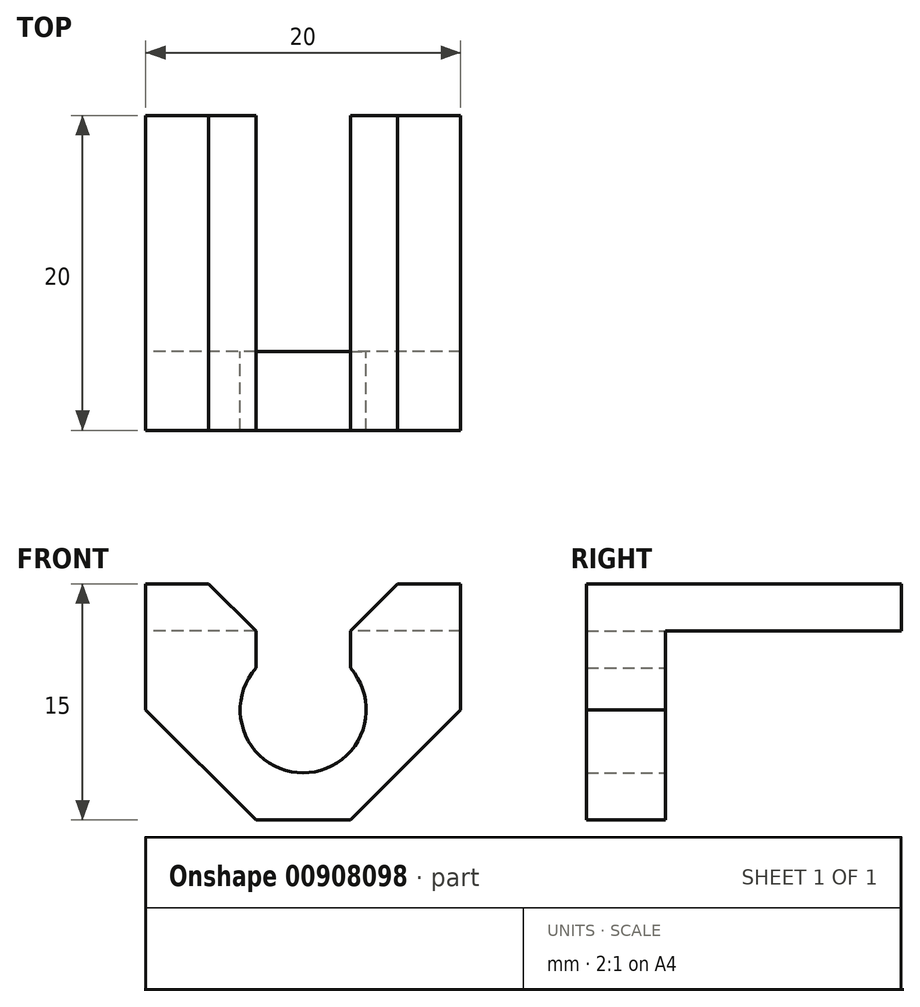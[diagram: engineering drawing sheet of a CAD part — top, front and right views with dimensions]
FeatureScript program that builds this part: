
annotation { "Feature Type Name" : "Feature", "Feature Type Description" : "" }
export const myFeature = defineFeature(function(context is Context, id is Id, definition is map)
    precondition{}
    {
        {
            var Q0;
            Q0=qCreatedBy(makeId("Front.planeOp"),FACE);
            var sketch = newSketch(context, id + "F0", { "sketchPlane" : qUnion([Q0])});
            skCircle(sketch, "E0", {"center": v(0, 0) * mm, "radius": 4 * mm});
            skLineSegment(sketch, "E1", {"start": v(0, -7) * mm, "end": v(10, -7) * mm});
            skLineSegment(sketch, "E2", {"start": v(10, -7) * mm, "end": v(10, 8) * mm});
            skLineSegment(sketch, "E3", {"start": v(10, 8) * mm, "end": v(3, 8) * mm});
            skLineSegment(sketch, "E4", {"start": v(3, 8) * mm, "end": v(3, 2.65) * mm});
            skLineSegment(sketch, "E5.MirrorCS", {"start": v(-3, 8) * mm, "end": v(-3, 2.65) * mm});
            skLineSegment(sketch, "E6.MirrorCS", {"start": v(-10, 8) * mm, "end": v(-3, 8) * mm});
            skLineSegment(sketch, "E7.MirrorCS", {"start": v(-10, -7) * mm, "end": v(-10, 8) * mm});
            skLineSegment(sketch, "E8.MirrorCS", {"start": v(0, -7) * mm, "end": v(-10, -7) * mm});
            skSolve(sketch);
        }
        {
            var Q0;
            Q0=makeQuery(id+"F0.imprint","IMPRINT",FACE,{"disambiguationData":[TD([[makeQuery(id+"F0.imprint","IMPRINT",EDGE,{"derivedFrom":sQuery(id+"F0.wireOp",EDGE,"E1")}),1.0]])]});
            extrude(context, id + "F1", {"entities" : qUnion([Q0]), "depth" : 5 * mm, "offsetDistance" : 25 * mm});
        }
        {
            var Q0;
            Q0=makeQuery(id+"F1.opExtrude","SWEPT_EDGE",EDGE,{"disambiguationData":[OSD([sQuery(id+"F0.wireOp",EDGE,"E7.MirrorCS"),sQuery(id+"F0.wireOp",EDGE,"E8.MirrorCS")])]});
            var Q1;
            Q1=makeQuery(id+"F1.opExtrude","SWEPT_EDGE",EDGE,{"disambiguationData":[OSD([sQuery(id+"F0.wireOp",EDGE,"E1"),sQuery(id+"F0.wireOp",EDGE,"E2")])]});
            chamfer(context, id + "F2", {"entities" : qUnion([Q0, Q1]), "width" : 7 * mm, "tangentPropagation" : true});
        }
        {
            var Q0;
            Q0=makeQuery(id+"F1.opExtrude","CAP_FACE",FACE,{"disambiguationData":[OSD([sQuery(id+"F0.wireOp",EDGE,"E0"),sQuery(id+"F0.wireOp",EDGE,"E1"),sQuery(id+"F0.wireOp",EDGE,"E2"),sQuery(id+"F0.wireOp",EDGE,"E3"),sQuery(id+"F0.wireOp",EDGE,"E4"),sQuery(id+"F0.wireOp",EDGE,"E5.MirrorCS"),sQuery(id+"F0.wireOp",EDGE,"E6.MirrorCS"),sQuery(id+"F0.wireOp",EDGE,"E7.MirrorCS"),sQuery(id+"F0.wireOp",EDGE,"E8.MirrorCS")])],"isStart":true});
            var sketch = newSketch(context, id + "F3", { "sketchPlane" : qUnion([Q0])});
            skLineSegment(sketch, "E9.0.0", {"start": v(-10, 8) * mm, "end": v(-10, 0) * mm});
            skLineSegment(sketch, "E9.0.1", {"start": v(-10, 0) * mm, "end": v(-3, -7) * mm});
            skLineSegment(sketch, "E9.0.2", {"start": v(-3, -7) * mm, "end": v(3, -7) * mm});
            skLineSegment(sketch, "E9.0.3", {"start": v(3, -7) * mm, "end": v(10, 0) * mm});
            skLineSegment(sketch, "E9.0.4", {"start": v(10, 0) * mm, "end": v(10, 8) * mm});
            skLineSegment(sketch, "E9.0.5", {"start": v(10, 8) * mm, "end": v(3, 8) * mm});
            skLineSegment(sketch, "E9.0.6", {"start": v(3, 8) * mm, "end": v(3, 2.65) * mm});
            skArc(sketch, "E9.0.7", {"start": v(3, 2.65) * mm, "mid": v(0, -4) * mm, "end": v(-3, 2.65) * mm});
            skLineSegment(sketch, "E9.0.8", {"start": v(-3, 2.65) * mm, "end": v(-3, 8) * mm});
            skLineSegment(sketch, "E9.0.9", {"start": v(-3, 8) * mm, "end": v(-10, 8) * mm});
            skLineSegment(sketch, "E10", {"start": v(-10, 5) * mm, "end": v(10, 5) * mm});
            skSolve(sketch);
        }
        {
            var Q0;
            {var subQ0=sQuery(id+"F3.wireOp",EDGE,"E9.0.9");Q0=makeQuery(id+"F3.imprint","IMPRINT",FACE,{"disambiguationData":[TD([[makeQuery(id+"F3.imprint","IMPRINT",EDGE,{"derivedFrom":subQ0}),-1.0]])]});}
            var Q1;
            {var subQ0=sQuery(id+"F3.wireOp",EDGE,"E9.0.5");Q1=makeQuery(id+"F3.imprint","IMPRINT",FACE,{"disambiguationData":[TD([[makeQuery(id+"F3.imprint","IMPRINT",EDGE,{"derivedFrom":subQ0}),1.0]])]});}
            extrude(context, id + "F4", {"entities" : qUnion([Q0, Q1]), "operationType" : NewBodyOperationType.ADD, "depth" : 15 * mm, "offsetDistance" : 25 * mm});
        }
        {
            var Q0;
            Q0=makeQuery(id+"F4.boolean.opBoolean","MERGE",EDGE,{"derivedFrom":[makeQuery(id+"F1.opExtrude","SWEPT_EDGE",EDGE,{"disambiguationData":[OSD([sQuery(id+"F0.wireOp",EDGE,"E5.MirrorCS"),sQuery(id+"F0.wireOp",EDGE,"E6.MirrorCS")])]}),makeQuery(id+"F4.opExtrude","SWEPT_EDGE",EDGE,{"disambiguationData":[OSD([sQuery(id+"F3.wireOp",EDGE,"E9.0.5"),sQuery(id+"F3.wireOp",EDGE,"E9.0.6")])]})]});
            var Q1;
            Q1=makeQuery(id+"F4.boolean.opBoolean","MERGE",EDGE,{"derivedFrom":[makeQuery(id+"F1.opExtrude","SWEPT_EDGE",EDGE,{"disambiguationData":[OSD([sQuery(id+"F0.wireOp",EDGE,"E3"),sQuery(id+"F0.wireOp",EDGE,"E4")])]}),makeQuery(id+"F4.opExtrude","SWEPT_EDGE",EDGE,{"disambiguationData":[OSD([sQuery(id+"F3.wireOp",EDGE,"E9.0.8"),sQuery(id+"F3.wireOp",EDGE,"E9.0.9")])]})]});
            chamfer(context, id + "F5", {"entities" : qUnion([Q0, Q1]), "width" : 3 * mm, "tangentPropagation" : true});
        }
    });
